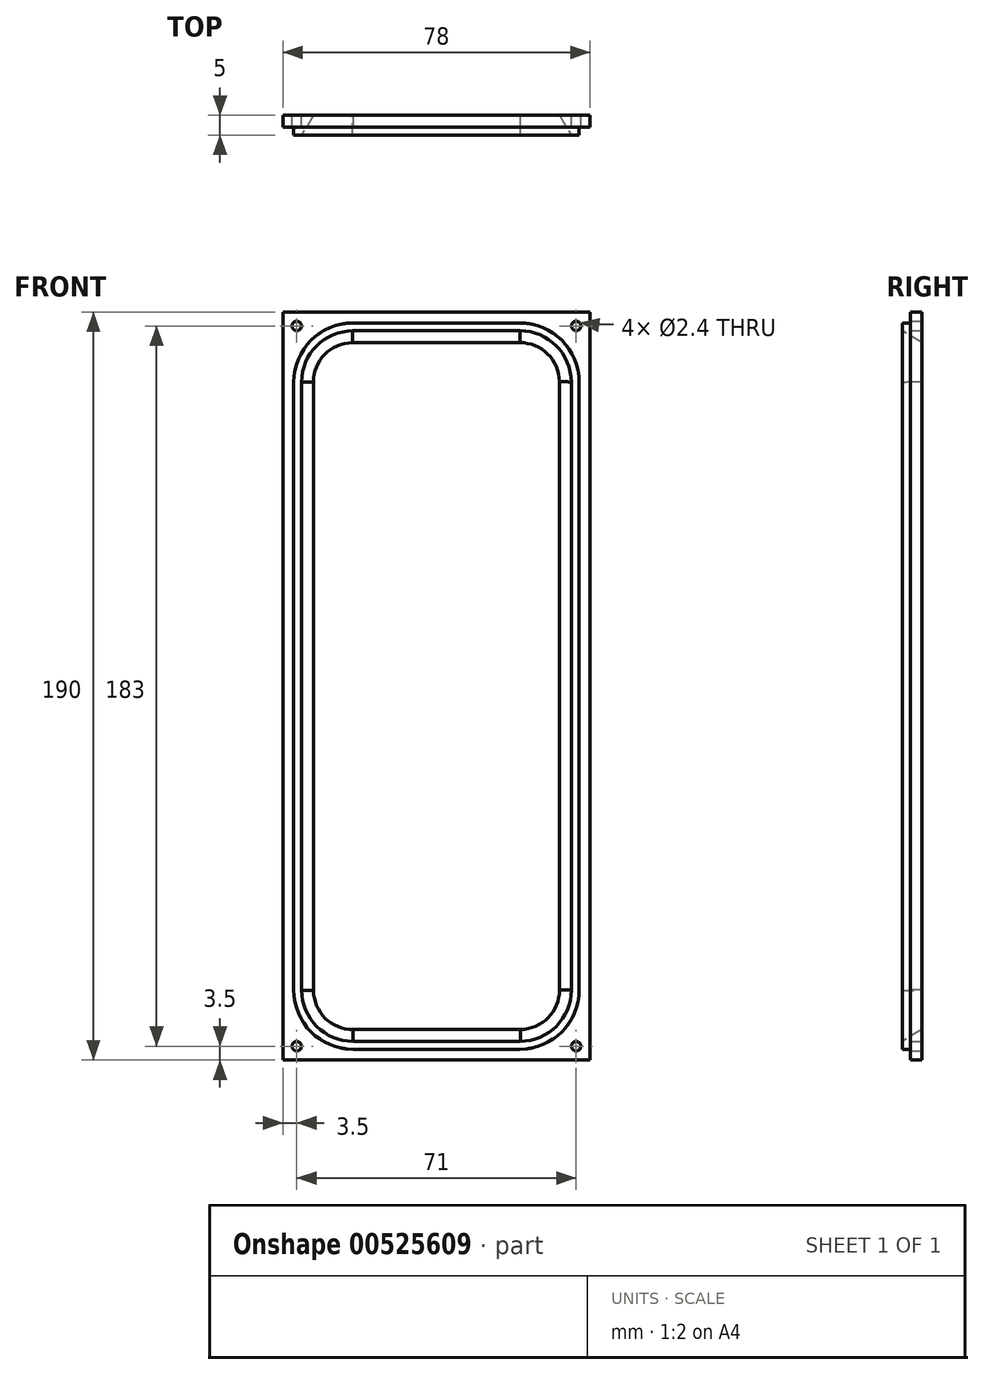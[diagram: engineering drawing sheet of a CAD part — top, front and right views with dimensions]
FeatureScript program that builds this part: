
annotation { "Feature Type Name" : "Feature", "Feature Type Description" : "" }
export const myFeature = defineFeature(function(context is Context, id is Id, definition is map)
    precondition{}
    {
        {
            var Q0;
            Q0=qCreatedBy(makeId("Front.planeOp"),FACE);
            var sketch = newSketch(context, id + "F0", { "sketchPlane" : qUnion([Q0])});
            skLineSegment(sketch, "E0.bottom", {"start": v(39, -95) * mm, "end": v(-39, -95) * mm});
            skLineSegment(sketch, "E0.top", {"start": v(39, 95) * mm, "end": v(-39, 95) * mm});
            skLineSegment(sketch, "E0.left", {"start": v(39, -95) * mm, "end": v(39, 95) * mm});
            skLineSegment(sketch, "E0.right", {"start": v(-39, -95) * mm, "end": v(-39, 95) * mm});
            skPoint(sketch, "E0.middle", {"position": v(0, 0) * mm});
            skLineSegment(sketch, "E1.bottom", {"start": v(21.25, -92.25) * mm, "end": v(-21.25, -92.25) * mm});
            skLineSegment(sketch, "E1.top", {"start": v(21.25, 92.25) * mm, "end": v(-21.25, 92.25) * mm});
            skLineSegment(sketch, "E1.left", {"start": v(36.25, -77.25) * mm, "end": v(36.25, 77.25) * mm});
            skLineSegment(sketch, "E1.right", {"start": v(-36.25, -77.25) * mm, "end": v(-36.25, 77.25) * mm});
            skPoint(sketch, "E2.visualSharp", {"position": v(-36.25, 92.25) * mm});
            skArc(sketch, "E2.filletArc", {"start": v(-21.25, 92.25) * mm, "mid": v(-31.86, 87.86) * mm, "end": v(-36.25, 77.25) * mm});
            skPoint(sketch, "E3.visualSharp", {"position": v(36.25, 92.25) * mm});
            skArc(sketch, "E3.filletArc", {"start": v(36.25, 77.25) * mm, "mid": v(31.86, 87.86) * mm, "end": v(21.25, 92.25) * mm});
            skPoint(sketch, "E4.visualSharp", {"position": v(-36.25, -92.25) * mm});
            skArc(sketch, "E4.filletArc", {"start": v(-36.25, -77.25) * mm, "mid": v(-31.86, -87.86) * mm, "end": v(-21.25, -92.25) * mm});
            skPoint(sketch, "E5.visualSharp", {"position": v(36.25, -92.25) * mm});
            skArc(sketch, "E5.filletArc", {"start": v(21.25, -92.25) * mm, "mid": v(31.86, -87.86) * mm, "end": v(36.25, -77.25) * mm});
            skCircle(sketch, "E6", {"center": v(-35.5, 91.5) * mm, "radius": 1.2 * mm});
            skCircle(sketch, "E7", {"center": v(35.5, 91.5) * mm, "radius": 1.2 * mm});
            skCircle(sketch, "E8", {"center": v(-35.5, -91.5) * mm, "radius": 1.2 * mm});
            skCircle(sketch, "E9", {"center": v(35.5, -91.5) * mm, "radius": 1.2 * mm});
            skLineSegment(sketch, "E10.bottom", {"start": v(805.8, -160.26) * mm, "end": v(670.8, -160.26) * mm});
            skLineSegment(sketch, "E10.top", {"start": v(805.8, 56.74) * mm, "end": v(670.8, 56.74) * mm});
            skLineSegment(sketch, "E10.left", {"start": v(805.8, -160.26) * mm, "end": v(805.8, 56.74) * mm});
            skLineSegment(sketch, "E10.right", {"start": v(670.8, -160.26) * mm, "end": v(670.8, 56.74) * mm});
            skPoint(sketch, "E10.middle", {"position": v(738.3, -51.76) * mm});
            skLineSegment(sketch, "E11.bottom", {"start": v(303.6, 275.23) * mm, "end": v(149.6, 275.23) * mm});
            skLineSegment(sketch, "E11.top", {"start": v(303.6, 361.23) * mm, "end": v(149.6, 361.23) * mm});
            skLineSegment(sketch, "E11.left", {"start": v(303.6, 275.23) * mm, "end": v(303.6, 361.23) * mm});
            skLineSegment(sketch, "E11.right", {"start": v(149.6, 275.23) * mm, "end": v(149.6, 361.23) * mm});
            skPoint(sketch, "E11.middle", {"position": v(226.6, 318.23) * mm});
            skLineSegment(sketch, "E12.bottom", {"start": v(760.26, 270.73) * mm, "end": v(639.26, 270.73) * mm});
            skLineSegment(sketch, "E12.top", {"start": v(760.26, 346.73) * mm, "end": v(639.26, 346.73) * mm});
            skLineSegment(sketch, "E12.left", {"start": v(760.26, 270.73) * mm, "end": v(760.26, 346.73) * mm});
            skLineSegment(sketch, "E12.right", {"start": v(639.26, 270.73) * mm, "end": v(639.26, 346.73) * mm});
            skPoint(sketch, "E12.middle", {"position": v(699.76, 308.73) * mm});
            skLineSegment(sketch, "E13.bottom", {"start": v(659.42, -327.35) * mm, "end": v(583.42, -327.35) * mm});
            skLineSegment(sketch, "E13.top", {"start": v(659.42, -206.35) * mm, "end": v(583.42, -206.35) * mm});
            skLineSegment(sketch, "E13.left", {"start": v(659.42, -327.35) * mm, "end": v(659.42, -206.35) * mm});
            skLineSegment(sketch, "E13.right", {"start": v(583.42, -327.35) * mm, "end": v(583.42, -206.35) * mm});
            skPoint(sketch, "E13.middle", {"position": v(621.42, -266.85) * mm});
            skLineSegment(sketch, "E14.bottom", {"start": v(547.19, -165.95) * mm, "end": v(330.19, -165.95) * mm});
            skLineSegment(sketch, "E14.top", {"start": v(547.19, -30.95) * mm, "end": v(330.19, -30.95) * mm});
            skLineSegment(sketch, "E14.left", {"start": v(547.19, -165.95) * mm, "end": v(547.19, -30.95) * mm});
            skLineSegment(sketch, "E14.right", {"start": v(330.19, -165.95) * mm, "end": v(330.19, -30.95) * mm});
            skPoint(sketch, "E14.middle", {"position": v(438.69, -98.45) * mm});
            skSolve(sketch);
        }
        {
            var Q0;
            Q0=makeQuery(id+"F0.imprint","IMPRINT",FACE,{"disambiguationData":[TD([[makeQuery(id+"F0.imprint","IMPRINT",EDGE,{"derivedFrom":sQuery(id+"F0.wireOp",EDGE,"E0.bottom")}),-1.0]])]});
            extrude(context, id + "F1", {"entities" : qUnion([Q0]), "depth" : 3 * mm, "offsetDistance" : 25 * mm});
        }
        {
            var Q0;
            Q0=qCreatedBy(makeId("Top.planeOp"),FACE);
            cPlane(context, id + "F2", {"entities" : qUnion([Q0]), "cplaneType" : CPlaneType.OFFSET, "offset" : 77.5 * mm, "oppositeDirection" : true, "width" : 150 * mm, "height" : 150 * mm});
        }
        {
            var Q0;
            Q0=qCreatedBy(id+"F2.planeOp",FACE);
            var sketch = newSketch(context, id + "F3", { "sketchPlane" : qUnion([Q0])});
            skLineSegment(sketch, "E15", {"start": v(-36.25, -5) * mm, "end": v(-36.25, 0) * mm});
            skLineSegment(sketch, "E16", {"start": v(-36.25, 0) * mm, "end": v(-31.25, 0) * mm});
            skLineSegment(sketch, "E17", {"start": v(-31.25, 0) * mm, "end": v(-34.25, -5) * mm});
            skLineSegment(sketch, "E18", {"start": v(-34.25, -5) * mm, "end": v(-36.25, -5) * mm});
            skSolve(sketch);
        }
        {
            var Q0;
            Q0=qSketchRegion(id+"F3",true);
            var Q1;
            Q1=sQuery(id+"F0.wireOp",EDGE,"E1.right");
            var Q2;
            Q2=sQuery(id+"F0.wireOp",EDGE,"E2.filletArc");
            var Q3;
            Q3=sQuery(id+"F0.wireOp",EDGE,"E1.top");
            var Q4;
            Q4=sQuery(id+"F0.wireOp",EDGE,"E3.filletArc");
            var Q5;
            Q5=sQuery(id+"F0.wireOp",EDGE,"E1.left");
            var Q6;
            Q6=sQuery(id+"F0.wireOp",EDGE,"E5.filletArc");
            var Q7;
            Q7=sQuery(id+"F0.wireOp",EDGE,"E1.bottom");
            var Q8;
            Q8=sQuery(id+"F0.wireOp",EDGE,"E4.filletArc");
            sweep(context, id + "F4", {"operationType" : NewBodyOperationType.ADD, "profiles" : qUnion([Q0]), "path" : qUnion([Q1, Q2, Q3, Q4, Q5, Q6, Q7, Q8])});
        }
    });
